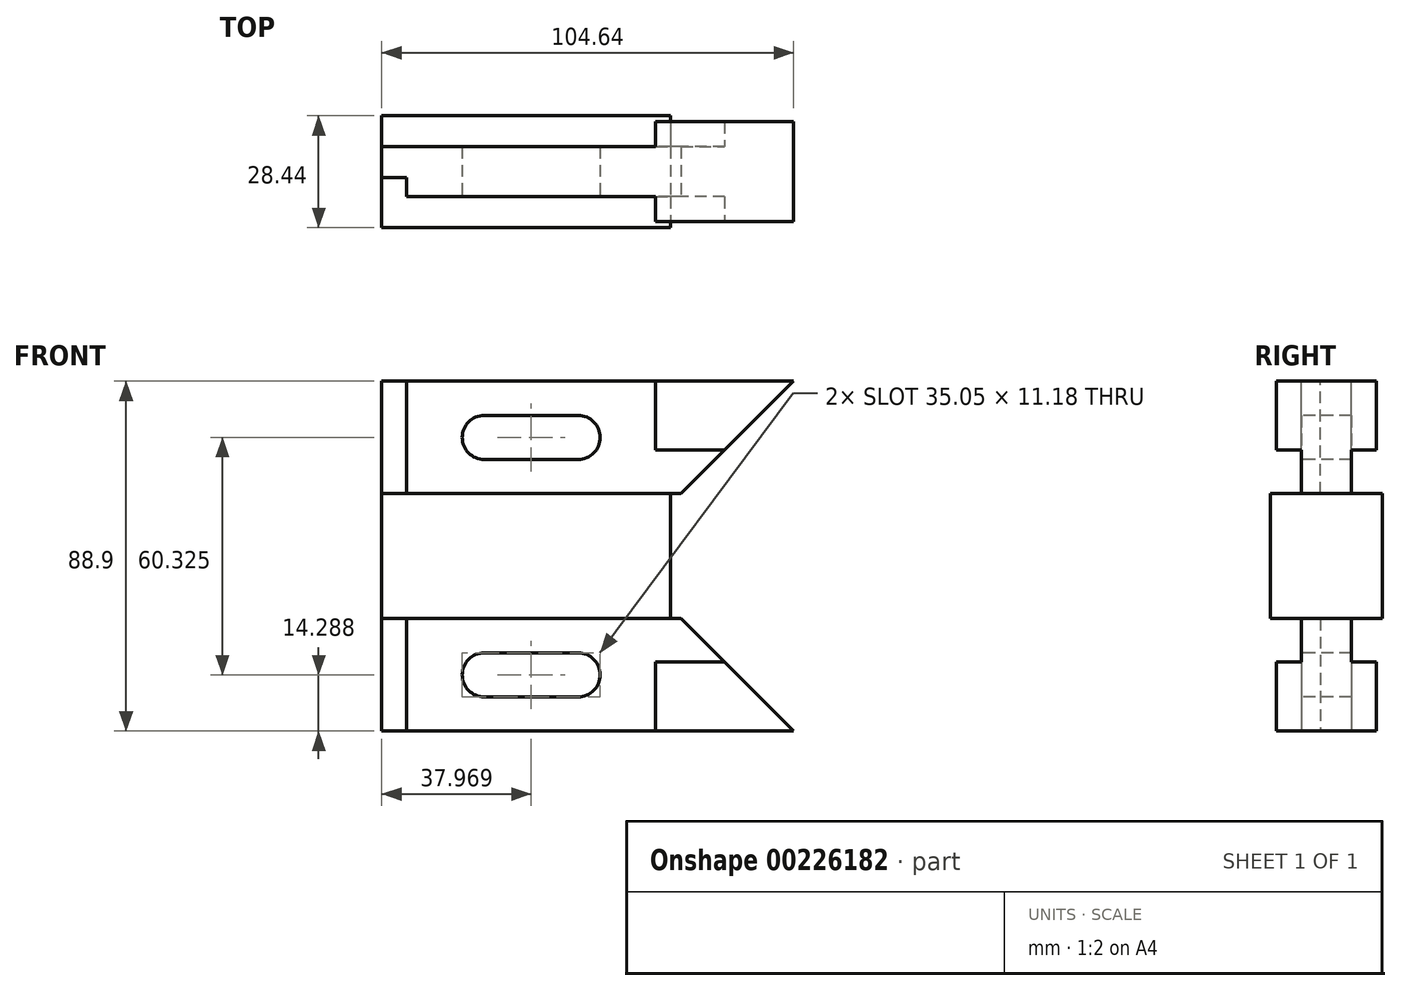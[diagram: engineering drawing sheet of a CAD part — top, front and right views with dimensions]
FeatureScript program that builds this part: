
annotation { "Feature Type Name" : "Feature", "Feature Type Description" : "" }
export const myFeature = defineFeature(function(context is Context, id is Id, definition is map)
    precondition{}
    {
        {
            var Q0;
            Q0=qCreatedBy(makeId("Front.planeOp"),FACE);
            var sketch = newSketch(context, id + "F0", { "sketchPlane" : qUnion([Q0])});
            skLineSegment(sketch, "E0.bottom", {"start": v(52.32, 44.45) * mm, "end": v(-52.32, 44.45) * mm});
            skLineSegment(sketch, "E0.top", {"start": v(52.32, -44.45) * mm, "end": v(-52.32, -44.45) * mm});
            skLineSegment(sketch, "E0.left", {"start": v(52.32, 44.45) * mm, "end": v(52.32, -44.45) * mm});
            skLineSegment(sketch, "E0.right", {"start": v(-52.32, 44.45) * mm, "end": v(-52.32, -44.45) * mm});
            skPoint(sketch, "E0.middle", {"position": v(0, 0) * mm});
            skSolve(sketch);
        }
        {
            var Q0;
            Q0 = qSketchRegion(id + "F0", true);
            extrude(context, id + "F1", {"entities" : qUnion([Q0]), "endBound" : BoundingType.SYMMETRIC, "depth" : 25.4 * mm});
        }
        {
            var Q0;
            Q0=makeQuery(id+"F1.opExtrude","SWEPT_FACE",FACE,{"disambiguationData":[OSD([sQuery(id+"F0.wireOp",EDGE,"E0.bottom")])]});
            var sketch = newSketch(context, id + "F2", { "sketchPlane" : qUnion([Q0])});
            skLineSegment(sketch, "E1", {"start": v(-52.32, 6.35) * mm, "end": v(17.27, 6.35) * mm});
            skLineSegment(sketch, "E2", {"start": v(17.27, 6.35) * mm, "end": v(17.27, 12.7) * mm});
            skLineSegment(sketch, "E3", {"start": v(-52.32, -1.52) * mm, "end": v(-45.97, -1.52) * mm});
            skLineSegment(sketch, "E4", {"start": v(-45.97, -1.52) * mm, "end": v(-45.97, -6.35) * mm});
            skLineSegment(sketch, "E5", {"start": v(-45.97, -6.35) * mm, "end": v(17.27, -6.35) * mm});
            skLineSegment(sketch, "E6", {"start": v(17.27, -6.35) * mm, "end": v(17.27, -12.7) * mm});
            skSolve(sketch);
        }
        {
            var Q0;
            {var subQ0=sQuery(id+"F2.wireOp",EDGE,"E1");Q0=makeQuery(id+"F2.imprint","IMPRINT",FACE,{"disambiguationData":[TD([[makeQuery(id+"F2.imprint","IMPRINT",EDGE,{"derivedFrom":subQ0}),1.0]])]});}
            var Q1;
            {var subQ1=sQuery(id+"F2.wireOp",EDGE,"E3");Q1=makeQuery(id+"F2.imprint","IMPRINT",FACE,{"disambiguationData":[TD([[makeQuery(id+"F2.imprint","IMPRINT",EDGE,{"derivedFrom":subQ1}),-1.0]])]});}
            extrude(context, id + "F3", {"entities" : qUnion([Q0, Q1]), "operationType" : NewBodyOperationType.REMOVE, "oppositeDirection" : true, "depth" : 28.57 * mm});
        }
        {
            var Q0;
            Q0=makeQuery(id+"F1.opExtrude","SWEPT_FACE",FACE,{"disambiguationData":[OSD([sQuery(id+"F0.wireOp",EDGE,"E0.top")])]});
            var sketch = newSketch(context, id + "F4", { "sketchPlane" : qUnion([Q0])});
            skLineSegment(sketch, "E7", {"start": v(17.27, 6.35) * mm, "end": v(17.27, 12.7) * mm});
            skLineSegment(sketch, "E8", {"start": v(-52.32, -6.35) * mm, "end": v(17.27, -6.35) * mm});
            skLineSegment(sketch, "E9", {"start": v(17.27, -6.35) * mm, "end": v(17.27, -12.7) * mm});
            skLineSegment(sketch, "E10", {"start": v(17.27, 6.35) * mm, "end": v(-45.97, 6.35) * mm});
            skLineSegment(sketch, "E11", {"start": v(-45.97, 6.35) * mm, "end": v(-45.97, 1.52) * mm});
            skLineSegment(sketch, "E12", {"start": v(-45.97, 1.52) * mm, "end": v(-52.32, 1.52) * mm});
            skSolve(sketch);
        }
        {
            var Q0;
            {var subQ1=sQuery(id+"F4.wireOp",EDGE,"E7");Q0=makeQuery(id+"F4.imprint","IMPRINT",FACE,{"disambiguationData":[TD([[makeQuery(id+"F4.imprint","IMPRINT",EDGE,{"derivedFrom":subQ1}),1.0]])]});}
            var Q1;
            {var subQ0=sQuery(id+"F4.wireOp",EDGE,"E8");Q1=makeQuery(id+"F4.imprint","IMPRINT",FACE,{"disambiguationData":[TD([[makeQuery(id+"F4.imprint","IMPRINT",EDGE,{"derivedFrom":subQ0}),-1.0]])]});}
            extrude(context, id + "F5", {"entities" : qUnion([Q0, Q1]), "operationType" : NewBodyOperationType.REMOVE, "oppositeDirection" : true, "depth" : 28.57 * mm});
        }
        {
            var Q0;
            Q0=makeQuery(id+"F1.opExtrude","SWEPT_FACE",FACE,{"disambiguationData":[OSD([sQuery(id+"F0.wireOp",EDGE,"E0.left")])]});
            var sketch = newSketch(context, id + "F6", { "sketchPlane" : qUnion([Q0])});
            skLineSegment(sketch, "E13", {"start": v(-12.7, 15.87) * mm, "end": v(12.7, 15.87) * mm});
            skLineSegment(sketch, "E14", {"start": v(-12.7, -15.88) * mm, "end": v(12.7, -15.87) * mm});
            skLineSegment(sketch, "E15.0", {"start": v(-12.7, 44.45) * mm, "end": v(-12.7, -44.45) * mm});
            skLineSegment(sketch, "E16.0", {"start": v(12.7, 44.45) * mm, "end": v(12.7, -44.45) * mm});
            skSolve(sketch);
        }
        {
            var Q0;
            Q0=makeQuery(id+"F1.opExtrude","CAP_FACE",FACE,{"disambiguationData":[OSD([sQuery(id+"F0.wireOp",EDGE,"E0.bottom"),sQuery(id+"F0.wireOp",EDGE,"E0.top"),sQuery(id+"F0.wireOp",EDGE,"E0.left"),sQuery(id+"F0.wireOp",EDGE,"E0.right")])],"isStart":false});
            var sketch = newSketch(context, id + "F7", { "sketchPlane" : qUnion([Q0])});
            skPoint(sketch, "E17.0", {"position": v(52.32, 15.87) * mm});
            skLineSegment(sketch, "E18", {"start": v(52.32, 15.87) * mm, "end": v(17.27, 15.87) * mm});
            skPoint(sketch, "E19.0", {"position": v(52.32, -15.88) * mm});
            skLineSegment(sketch, "E20", {"start": v(52.32, -15.88) * mm, "end": v(17.27, -15.88) * mm});
            skLineSegment(sketch, "E21.0", {"start": v(52.32, 44.45) * mm, "end": v(52.32, -44.45) * mm});
            skSolve(sketch);
        }
        {
            var Q0;
            Q0=makeQuery(id+"F1.opExtrude","SWEPT_FACE",FACE,{"disambiguationData":[OSD([sQuery(id+"F0.wireOp",EDGE,"E0.right")])]});
            var sketch = newSketch(context, id + "F8", { "sketchPlane" : qUnion([Q0])});
            skLineSegment(sketch, "E22", {"start": v(12.7, 15.87) * mm, "end": v(-12.7, 15.87) * mm});
            skLineSegment(sketch, "E23.0", {"start": v(-12.7, 44.45) * mm, "end": v(-12.7, -44.45) * mm});
            skLineSegment(sketch, "E24.0", {"start": v(12.7, 44.45) * mm, "end": v(12.7, -44.45) * mm});
            skLineSegment(sketch, "E25", {"start": v(-12.7, -15.88) * mm, "end": v(12.7, -15.88) * mm});
            skSolve(sketch);
        }
        {
            var Q0;
            Q0=makeQuery(id+"F1.opExtrude","CAP_FACE",FACE,{"disambiguationData":[OSD([sQuery(id+"F0.wireOp",EDGE,"E0.bottom"),sQuery(id+"F0.wireOp",EDGE,"E0.top"),sQuery(id+"F0.wireOp",EDGE,"E0.left"),sQuery(id+"F0.wireOp",EDGE,"E0.right")])],"isStart":true});
            var sketch = newSketch(context, id + "F9", { "sketchPlane" : qUnion([Q0])});
            skLineSegment(sketch, "E26", {"start": v(-17.27, 15.87) * mm, "end": v(-52.32, 15.87) * mm});
            skLineSegment(sketch, "E27.0", {"start": v(-52.32, 44.45) * mm, "end": v(-52.32, -44.45) * mm});
            skLineSegment(sketch, "E28", {"start": v(-17.27, -15.87) * mm, "end": v(-52.32, -15.88) * mm});
            skSolve(sketch);
        }
        {
            var Q0;
            {var subQ5=sQuery(id+"F9.wireOp",EDGE,"E26");Q0=makeQuery(id+"F9.imprint","IMPRINT",FACE,{"disambiguationData":[TD([[makeQuery(id+"F9.imprint","IMPRINT",EDGE,{"derivedFrom":subQ5}),1.0]])]});}
            var Q1;
            {var subQ4=sQuery(id+"F7.wireOp",EDGE,"E18");Q1=makeQuery(id+"F7.imprint","IMPRINT",FACE,{"disambiguationData":[TD([[makeQuery(id+"F7.imprint","IMPRINT",EDGE,{"derivedFrom":subQ4}),1.0]])]});}
            extrude(context, id + "F10", {"entities" : qUnion([Q0, Q1]), "operationType" : NewBodyOperationType.ADD, "endBound" : BoundingType.SYMMETRIC, "depth" : 3.05 * mm});
        }
        {
            var Q0;
            Q0=makeQuery(id+"F10.opExtrude","CAP_FACE",FACE,{"disambiguationData":[OSD([sQuery(id+"F0.wireOp",EDGE,"E0.bottom"),sQuery(id+"F0.wireOp",EDGE,"E0.top"),sQuery(id+"F0.wireOp",EDGE,"E0.right"),sQuery(id+"F7.wireOp",EDGE,"E18"),sQuery(id+"F7.wireOp",EDGE,"E20"),sQuery(id+"F7.wireOp",EDGE,"E21.0")])],"isStart":true});
            var sketch = newSketch(context, id + "F11", { "sketchPlane" : qUnion([Q0])});
            skLineSegment(sketch, "E29", {"start": v(21.08, 15.87) * mm, "end": v(21.08, -15.88) * mm});
            skLineSegment(sketch, "E30.0", {"start": v(52.32, 15.87) * mm, "end": v(-52.32, 15.87) * mm});
            skLineSegment(sketch, "E31.0", {"start": v(52.32, -15.88) * mm, "end": v(-52.32, -15.88) * mm});
            skSolve(sketch);
        }
        {
            var Q0;
            {var subQ0=sQuery(id+"F11.wireOp",EDGE,"E29");Q0=makeQuery(id+"F11.imprint","IMPRINT",FACE,{"disambiguationData":[TD([[makeQuery(id+"F11.imprint","IMPRINT",EDGE,{"derivedFrom":subQ0}),1.0]])]});}
            extrude(context, id + "F12", {"entities" : qUnion([Q0]), "operationType" : NewBodyOperationType.REMOVE, "endBound" : BoundingType.THROUGH_ALL, "oppositeDirection" : true, "depth" : 25.4 * mm});
        }
        {
            var Q0;
            {var subQ1=sQuery(id+"F0.wireOp",EDGE,"E0.right");var subQ2=sQuery(id+"F0.wireOp",EDGE,"E0.bottom");var subQ3=sQuery(id+"F0.wireOp",EDGE,"E0.left");Q0=makeQuery(id+"F10.boolean.opBoolean","SPLIT",FACE,{"disambiguationData":[TD([makeQuery(id+"F1.opExtrude","SWEPT_FACE",FACE,{"disambiguationData":[OSD([subQ2])]})])],"derivedFrom":makeQuery(id+"F1.opExtrude","CAP_FACE",FACE,{"disambiguationData":[OSD([subQ2,sQuery(id+"F0.wireOp",EDGE,"E0.top"),subQ3,subQ1])],"isStart":false})});}
            var sketch = newSketch(context, id + "F13", { "sketchPlane" : qUnion([Q0])});
            skLineSegment(sketch, "E32", {"start": v(17.27, 26.92) * mm, "end": v(52.32, 26.92) * mm});
            skSolve(sketch);
        }
        {
            var Q0;
            Q0=makeQuery(id+"F3.boolean.opBoolean","COPY",FACE,{"derivedFrom":makeQuery(id+"F3.opExtrude","SWEPT_FACE",FACE,{"disambiguationData":[OSD([sQuery(id+"F2.wireOp",EDGE,"E6")])]})});
            var sketch = newSketch(context, id + "F14", { "sketchPlane" : qUnion([Q0])});
            skLineSegment(sketch, "E33.0", {"start": v(12.7, 15.87) * mm, "end": v(12.7, 44.45) * mm});
            skLineSegment(sketch, "E34.0", {"start": v(6.35, 15.87) * mm, "end": v(6.35, 44.45) * mm});
            skLineSegment(sketch, "E35", {"start": v(12.7, 26.92) * mm, "end": v(6.35, 26.92) * mm});
            skSolve(sketch);
        }
        {
            var Q0;
            {var subQ2=sQuery(id+"F14.wireOp",EDGE,"E35");Q0=makeQuery(id+"F14.imprint","IMPRINT",FACE,{"disambiguationData":[TD([[makeQuery(id+"F14.imprint","IMPRINT",EDGE,{"derivedFrom":subQ2}),1.0]])]});}
            extrude(context, id + "F15", {"entities" : qUnion([Q0]), "operationType" : NewBodyOperationType.REMOVE, "endBound" : BoundingType.THROUGH_ALL, "oppositeDirection" : true, "depth" : 25.4 * mm});
        }
        {
            var Q0;
            {var subQ1=sQuery(id+"F0.wireOp",EDGE,"E0.right");var subQ2=sQuery(id+"F0.wireOp",EDGE,"E0.bottom");var subQ3=sQuery(id+"F0.wireOp",EDGE,"E0.left");Q0=makeQuery(id+"F10.boolean.opBoolean","SPLIT",FACE,{"disambiguationData":[TD([makeQuery(id+"F1.opExtrude","SWEPT_FACE",FACE,{"disambiguationData":[OSD([subQ2])]})])],"derivedFrom":makeQuery(id+"F1.opExtrude","CAP_FACE",FACE,{"disambiguationData":[OSD([subQ2,sQuery(id+"F0.wireOp",EDGE,"E0.top"),subQ3,subQ1])],"isStart":true})});}
            var sketch = newSketch(context, id + "F16", { "sketchPlane" : qUnion([Q0])});
            skLineSegment(sketch, "E36", {"start": v(-52.32, 26.92) * mm, "end": v(-17.27, 26.92) * mm});
            skLineSegment(sketch, "E37.0", {"start": v(-17.27, 15.87) * mm, "end": v(-17.27, 44.45) * mm});
            skLineSegment(sketch, "E38.0", {"start": v(-52.32, 44.45) * mm, "end": v(-52.32, -44.45) * mm});
            skSolve(sketch);
        }
        {
            var Q0;
            Q0=makeQuery(id+"F3.boolean.opBoolean","COPY",FACE,{"derivedFrom":makeQuery(id+"F3.opExtrude","SWEPT_FACE",FACE,{"disambiguationData":[OSD([sQuery(id+"F2.wireOp",EDGE,"E2")])]})});
            var sketch = newSketch(context, id + "F17", { "sketchPlane" : qUnion([Q0])});
            skPoint(sketch, "E39.0", {"position": v(-12.7, 26.92) * mm});
            skLineSegment(sketch, "E40.0", {"start": v(-6.35, 15.87) * mm, "end": v(-6.35, 44.45) * mm});
            skLineSegment(sketch, "E41", {"start": v(-12.7, 26.92) * mm, "end": v(-6.35, 26.92) * mm});
            skSolve(sketch);
        }
        {
            var Q0;
            {var subQ1=sQuery(id+"F0.wireOp",EDGE,"E0.right");var subQ2=sQuery(id+"F0.wireOp",EDGE,"E0.top");var subQ3=sQuery(id+"F0.wireOp",EDGE,"E0.left");Q0=makeQuery(id+"F10.boolean.opBoolean","SPLIT",FACE,{"disambiguationData":[TD([makeQuery(id+"F1.opExtrude","SWEPT_FACE",FACE,{"disambiguationData":[OSD([subQ2])]})])],"derivedFrom":makeQuery(id+"F1.opExtrude","CAP_FACE",FACE,{"disambiguationData":[OSD([sQuery(id+"F0.wireOp",EDGE,"E0.bottom"),subQ2,subQ3,subQ1])],"isStart":true})});}
            var sketch = newSketch(context, id + "F18", { "sketchPlane" : qUnion([Q0])});
            skLineSegment(sketch, "E42", {"start": v(-17.27, -26.92) * mm, "end": v(-52.32, -26.92) * mm});
            skLineSegment(sketch, "E43.0", {"start": v(-17.27, -15.88) * mm, "end": v(-17.27, -44.45) * mm});
            skLineSegment(sketch, "E44.0", {"start": v(-52.32, 44.45) * mm, "end": v(-52.32, -44.45) * mm});
            skSolve(sketch);
        }
        {
            var Q0;
            Q0=makeQuery(id+"F5.boolean.opBoolean","COPY",FACE,{"derivedFrom":makeQuery(id+"F5.opExtrude","SWEPT_FACE",FACE,{"disambiguationData":[OSD([sQuery(id+"F4.wireOp",EDGE,"E9")])]})});
            var sketch = newSketch(context, id + "F19", { "sketchPlane" : qUnion([Q0])});
            skPoint(sketch, "E45.0", {"position": v(-12.7, -26.92) * mm});
            skLineSegment(sketch, "E46.0", {"start": v(-6.35, -15.88) * mm, "end": v(-6.35, -44.45) * mm});
            skLineSegment(sketch, "E47", {"start": v(-12.7, -26.92) * mm, "end": v(-6.35, -26.92) * mm});
            skSolve(sketch);
        }
        {
            var Q0;
            {var subQ3=sQuery(id+"F17.wireOp",EDGE,"E41");Q0=makeQuery(id+"F17.imprint","IMPRINT",FACE,{"disambiguationData":[TD([[makeQuery(id+"F17.imprint","IMPRINT",EDGE,{"derivedFrom":subQ3}),-1.0]])]});}
            extrude(context, id + "F20", {"entities" : qUnion([Q0]), "operationType" : NewBodyOperationType.REMOVE, "endBound" : BoundingType.THROUGH_ALL, "oppositeDirection" : true, "depth" : 25.4 * mm});
        }
        {
            var Q0;
            {var subQ3=sQuery(id+"F19.wireOp",EDGE,"E47");Q0=makeQuery(id+"F19.imprint","IMPRINT",FACE,{"disambiguationData":[TD([[makeQuery(id+"F19.imprint","IMPRINT",EDGE,{"derivedFrom":subQ3}),1.0]])]});}
            extrude(context, id + "F21", {"entities" : qUnion([Q0]), "operationType" : NewBodyOperationType.REMOVE, "endBound" : BoundingType.THROUGH_ALL, "oppositeDirection" : true, "depth" : 25.4 * mm});
        }
        {
            var Q0;
            Q0=makeQuery(id+"F5.boolean.opBoolean","COPY",FACE,{"derivedFrom":makeQuery(id+"F5.opExtrude","SWEPT_FACE",FACE,{"disambiguationData":[OSD([sQuery(id+"F4.wireOp",EDGE,"E7")])]})});
            var sketch = newSketch(context, id + "F22", { "sketchPlane" : qUnion([Q0])});
            skLineSegment(sketch, "E48", {"start": v(6.35, -26.92) * mm, "end": v(12.7, -26.92) * mm});
            skLineSegment(sketch, "E49.0", {"start": v(12.7, -15.88) * mm, "end": v(12.7, -44.45) * mm});
            skLineSegment(sketch, "E50.0", {"start": v(6.35, -15.88) * mm, "end": v(6.35, -44.45) * mm});
            skPoint(sketch, "E51.0", {"position": v(7.87, -15.88) * mm});
            skLineSegment(sketch, "E52.0", {"start": v(14.22, -15.88) * mm, "end": v(1.52, -15.88) * mm});
            skSolve(sketch);
        }
        {
            var Q0;
            {var subQ0=sQuery(id+"F22.wireOp",EDGE,"E48");Q0=makeQuery(id+"F22.imprint","IMPRINT",FACE,{"disambiguationData":[TD([[makeQuery(id+"F22.imprint","IMPRINT",EDGE,{"derivedFrom":subQ0}),1.0]])]});}
            extrude(context, id + "F23", {"entities" : qUnion([Q0]), "operationType" : NewBodyOperationType.REMOVE, "endBound" : BoundingType.THROUGH_ALL, "oppositeDirection" : true, "depth" : 25.4 * mm});
        }
        {
            var Q0;
            {var subQ1=sQuery(id+"F0.wireOp",EDGE,"E0.right");var subQ2=sQuery(id+"F0.wireOp",EDGE,"E0.top");var subQ3=sQuery(id+"F0.wireOp",EDGE,"E0.left");Q0=makeQuery(id+"F10.boolean.opBoolean","SPLIT",FACE,{"disambiguationData":[TD([makeQuery(id+"F1.opExtrude","SWEPT_FACE",FACE,{"disambiguationData":[OSD([subQ2])]})])],"derivedFrom":makeQuery(id+"F1.opExtrude","CAP_FACE",FACE,{"disambiguationData":[OSD([sQuery(id+"F0.wireOp",EDGE,"E0.bottom"),subQ2,subQ3,subQ1])],"isStart":false})});}
            var sketch = newSketch(context, id + "F24", { "sketchPlane" : qUnion([Q0])});
            skLineSegment(sketch, "E53", {"start": v(52.32, -44.45) * mm, "end": v(34.8, -26.92) * mm});
            skLineSegment(sketch, "E54", {"start": v(52.32, 44.45) * mm, "end": v(34.8, 26.92) * mm});
            skLineSegment(sketch, "E55.0.0", {"start": v(17.27, 26.92) * mm, "end": v(52.32, 26.92) * mm});
            skLineSegment(sketch, "E55.0.1", {"start": v(52.32, 26.92) * mm, "end": v(52.32, 44.45) * mm});
            skLineSegment(sketch, "E55.0.2", {"start": v(52.32, 44.45) * mm, "end": v(17.27, 44.45) * mm});
            skLineSegment(sketch, "E55.0.3", {"start": v(17.27, 44.45) * mm, "end": v(17.27, 26.92) * mm});
            skSolve(sketch);
        }
        {
            var Q0;
            {var subQ0=sQuery(id+"F24.wireOp",EDGE,"E54");Q0=makeQuery(id+"F24.imprint","IMPRINT",FACE,{"disambiguationData":[TD([[makeQuery(id+"F24.imprint","IMPRINT",EDGE,{"derivedFrom":subQ0}),1.0]])]});}
            var Q1;
            {var subQ0=sQuery(id+"F24.wireOp",EDGE,"E53");Q1=makeQuery(id+"F24.imprint","IMPRINT",FACE,{"disambiguationData":[TD([[makeQuery(id+"F24.imprint","IMPRINT",EDGE,{"derivedFrom":subQ0}),-1.0]])]});}
            extrude(context, id + "F25", {"entities" : qUnion([Q0, Q1]), "operationType" : NewBodyOperationType.REMOVE, "endBound" : BoundingType.THROUGH_ALL, "oppositeDirection" : true, "depth" : 25.4 * mm});
        }
        {
            var Q0;
            Q0=makeQuery(id+"F15.boolean.opBoolean","MERGE",FACE,{"derivedFrom":[makeQuery(id+"F3.boolean.opBoolean","COPY",FACE,{"derivedFrom":makeQuery(id+"F3.opExtrude","SWEPT_FACE",FACE,{"disambiguationData":[OSD([sQuery(id+"F2.wireOp",EDGE,"E5")])]})}),makeQuery(id+"F15.opExtrude","SWEPT_FACE",FACE,{"disambiguationData":[OSD([sQuery(id+"F14.wireOp",EDGE,"E34.0")])]})]});
            var sketch = newSketch(context, id + "F26", { "sketchPlane" : qUnion([Q0])});
            skLineSegment(sketch, "E56", {"start": v(34.8, 26.92) * mm, "end": v(23.75, 15.87) * mm});
            skLineSegment(sketch, "E57.0", {"start": v(52.32, -44.45) * mm, "end": v(34.8, -26.92) * mm});
            skLineSegment(sketch, "E58", {"start": v(34.8, -26.92) * mm, "end": v(23.75, -15.88) * mm});
            skLineSegment(sketch, "E59.0", {"start": v(52.32, -15.88) * mm, "end": v(21.08, -15.88) * mm});
            skLineSegment(sketch, "E60.0", {"start": v(52.32, 15.87) * mm, "end": v(21.08, 15.87) * mm});
            skLineSegment(sketch, "E61.0", {"start": v(52.32, 26.92) * mm, "end": v(17.27, 26.92) * mm});
            skLineSegment(sketch, "E62.0.0", {"start": v(-45.97, -44.45) * mm, "end": v(17.27, -44.45) * mm});
            skLineSegment(sketch, "E62.0.1", {"start": v(17.27, -44.45) * mm, "end": v(17.27, -26.92) * mm});
            skLineSegment(sketch, "E62.0.2", {"start": v(17.27, -26.92) * mm, "end": v(34.8, -26.92) * mm});
            skLineSegment(sketch, "E62.0.3", {"start": v(34.8, -26.92) * mm, "end": v(52.32, -26.92) * mm});
            skLineSegment(sketch, "E62.0.4", {"start": v(52.32, -26.92) * mm, "end": v(52.32, -15.88) * mm});
            skLineSegment(sketch, "E62.0.6", {"start": v(21.08, -15.88) * mm, "end": v(-45.97, -15.88) * mm});
            skLineSegment(sketch, "E62.0.7", {"start": v(-45.97, -15.88) * mm, "end": v(-45.97, -44.45) * mm});
            skSolve(sketch);
        }
        {
            var Q0;
            {var subQ0=sQuery(id+"F26.wireOp",EDGE,"E58");Q0=makeQuery(id+"F26.imprint","IMPRINT",FACE,{"disambiguationData":[TD([[makeQuery(id+"F26.imprint","IMPRINT",EDGE,{"derivedFrom":subQ0}),-1.0]])]});}
            var Q1;
            {var subQ0=sQuery(id+"F26.wireOp",EDGE,"E56");Q1=makeQuery(id+"F26.imprint","IMPRINT",FACE,{"disambiguationData":[TD([[makeQuery(id+"F26.imprint","IMPRINT",EDGE,{"derivedFrom":subQ0}),1.0]])]});}
            extrude(context, id + "F27", {"entities" : qUnion([Q0, Q1]), "operationType" : NewBodyOperationType.REMOVE, "endBound" : BoundingType.THROUGH_ALL, "oppositeDirection" : true, "depth" : 25.4 * mm});
        }
        {
            var Q0;
            Q0=makeQuery(id+"F15.boolean.opBoolean","MERGE",FACE,{"derivedFrom":[makeQuery(id+"F3.boolean.opBoolean","COPY",FACE,{"derivedFrom":makeQuery(id+"F3.opExtrude","SWEPT_FACE",FACE,{"disambiguationData":[OSD([sQuery(id+"F2.wireOp",EDGE,"E5")])]})}),makeQuery(id+"F15.opExtrude","SWEPT_FACE",FACE,{"disambiguationData":[OSD([sQuery(id+"F14.wireOp",EDGE,"E34.0")])]})]});
            var sketch = newSketch(context, id + "F28", { "sketchPlane" : qUnion([Q0])});
            skLineSegment(sketch, "E63.0", {"start": v(17.27, -15.88) * mm, "end": v(17.27, -44.45) * mm});
            skPoint(sketch, "E64.0", {"position": v(-45.97, -30.16) * mm});
            skPoint(sketch, "E65.0", {"position": v(17.27, -26.92) * mm});
            skLineSegment(sketch, "E66.0", {"start": v(-45.97, -15.88) * mm, "end": v(-45.97, -44.45) * mm});
            skLineSegment(sketch, "E67.0.0", {"start": v(17.27, -26.92) * mm, "end": v(34.8, -26.92) * mm});
            skLineSegment(sketch, "E67.0.1", {"start": v(34.8, -26.92) * mm, "end": v(23.75, -15.88) * mm});
            skLineSegment(sketch, "E67.0.2", {"start": v(23.75, -15.88) * mm, "end": v(21.08, -15.88) * mm});
            skLineSegment(sketch, "E67.0.3", {"start": v(21.08, -15.88) * mm, "end": v(-45.97, -15.88) * mm});
            skLineSegment(sketch, "E67.0.5", {"start": v(-45.97, -44.45) * mm, "end": v(17.27, -44.45) * mm});
            skLineSegment(sketch, "E67.0.6", {"start": v(17.27, -44.45) * mm, "end": v(17.27, -26.92) * mm});
            skCircle(sketch, "E68", {"center": v(-26.29, 30.16) * mm, "radius": 5.59 * mm});
            skCircle(sketch, "E69", {"center": v(-2.41, 30.16) * mm, "radius": 5.59 * mm});
            skLineSegment(sketch, "E70", {"start": v(-26.29, 35.75) * mm, "end": v(-2.41, 35.75) * mm});
            skLineSegment(sketch, "E71", {"start": v(-26.29, 24.57) * mm, "end": v(-2.41, 24.57) * mm});
            skCircle(sketch, "E72", {"center": v(-26.29, -30.16) * mm, "radius": 5.59 * mm});
            skCircle(sketch, "E73", {"center": v(-2.41, -30.16) * mm, "radius": 5.59 * mm});
            skLineSegment(sketch, "E74", {"start": v(-26.29, -24.57) * mm, "end": v(-2.41, -24.57) * mm});
            skLineSegment(sketch, "E75", {"start": v(-26.29, -35.75) * mm, "end": v(-2.41, -35.75) * mm});
            skLineSegment(sketch, "E76", {"start": v(-45.97, 30.16) * mm, "end": v(0, 30.16) * mm, "construction": true});
            skLineSegment(sketch, "E77", {"start": v(-45.97, -30.16) * mm, "end": v(0, -30.16) * mm, "construction": true});
            skSolve(sketch);
        }
        {
            var Q0;
            {var subQ0=sQuery(id+"F28.wireOp",EDGE,"E74");Q0=makeQuery(id+"F28.imprint","IMPRINT",FACE,{"disambiguationData":[TD([[makeQuery(id+"F28.imprint","IMPRINT",EDGE,{"derivedFrom":subQ0}),-1.0]])]});}
            var Q1;
            {var subQ0=sQuery(id+"F28.wireOp",EDGE,"E72");var subQ1=makeQuery(id+"F28.imprint","INTERSECT",VERTEX,{"derivedFrom":[subQ0,sQuery(id+"F28.wireOp",EDGE,"E74")]});Q1=makeQuery(id+"F28.imprint","IMPRINT",FACE,{"disambiguationData":[TD([[makeQuery(id+"F28.imprint","IMPRINT",EDGE,{"disambiguationData":[TD([[subQ1,-1.0]])],"derivedFrom":subQ0}),1.0]])]});}
            var Q2;
            {var subQ0=sQuery(id+"F28.wireOp",EDGE,"E73");var subQ1=makeQuery(id+"F28.imprint","INTERSECT",VERTEX,{"derivedFrom":[subQ0,sQuery(id+"F28.wireOp",EDGE,"E74")]});Q2=makeQuery(id+"F28.imprint","IMPRINT",FACE,{"disambiguationData":[TD([[makeQuery(id+"F28.imprint","IMPRINT",EDGE,{"disambiguationData":[TD([[subQ1,-1.0]])],"derivedFrom":subQ0}),1.0]])]});}
            var Q3;
            {var subQ0=sQuery(id+"F28.wireOp",EDGE,"E70");Q3=makeQuery(id+"F28.imprint","IMPRINT",FACE,{"disambiguationData":[TD([[makeQuery(id+"F28.imprint","IMPRINT",EDGE,{"derivedFrom":subQ0}),-1.0]])]});}
            var Q4;
            {var subQ0=sQuery(id+"F28.wireOp",EDGE,"E68");var subQ1=makeQuery(id+"F28.imprint","INTERSECT",VERTEX,{"derivedFrom":[subQ0,sQuery(id+"F28.wireOp",EDGE,"E70")]});Q4=makeQuery(id+"F28.imprint","IMPRINT",FACE,{"disambiguationData":[TD([[makeQuery(id+"F28.imprint","IMPRINT",EDGE,{"disambiguationData":[TD([[subQ1,-1.0]])],"derivedFrom":subQ0}),1.0]])]});}
            var Q5;
            {var subQ0=sQuery(id+"F28.wireOp",EDGE,"E69");var subQ1=makeQuery(id+"F28.imprint","INTERSECT",VERTEX,{"derivedFrom":[subQ0,sQuery(id+"F28.wireOp",EDGE,"E70")]});Q5=makeQuery(id+"F28.imprint","IMPRINT",FACE,{"disambiguationData":[TD([[makeQuery(id+"F28.imprint","IMPRINT",EDGE,{"disambiguationData":[TD([[subQ1,-1.0]])],"derivedFrom":subQ0}),1.0]])]});}
            extrude(context, id + "F29", {"entities" : qUnion([Q0, Q1, Q2, Q3, Q4, Q5]), "operationType" : NewBodyOperationType.REMOVE, "endBound" : BoundingType.THROUGH_ALL, "oppositeDirection" : true, "depth" : 25.4 * mm});
        }
    });
